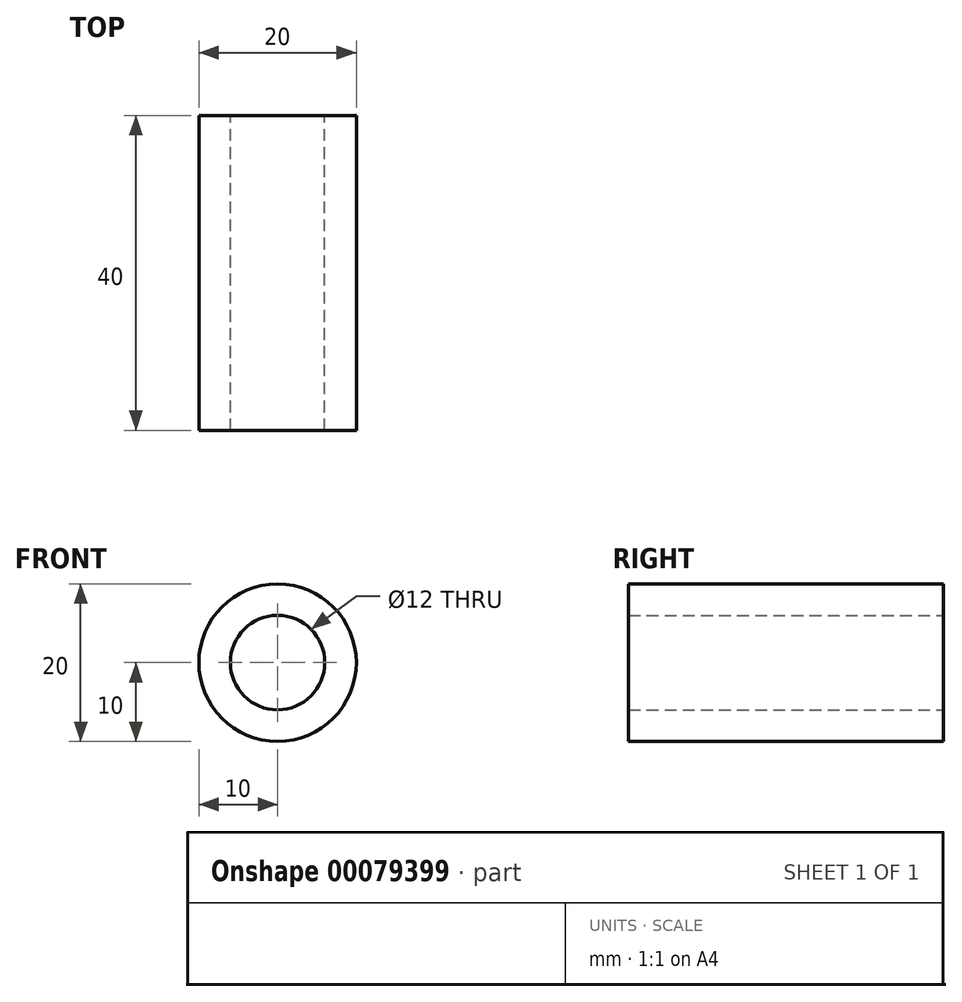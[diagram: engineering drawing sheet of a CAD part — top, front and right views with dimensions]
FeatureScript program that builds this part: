
annotation { "Feature Type Name" : "Feature", "Feature Type Description" : "" }
export const myFeature = defineFeature(function(context is Context, id is Id, definition is map)
    precondition{}
    {
        {
            var Q0;
            Q0=qCreatedBy(makeId("Front.planeOp"),FACE);
            var sketch = newSketch(context, id + "F0", { "sketchPlane" : qUnion([Q0])});
            skCircle(sketch, "E0", {"center": v(0, 0) * mm, "radius": 10 * mm});
            skCircle(sketch, "E1", {"center": v(0, 0) * mm, "radius": 6 * mm});
            skSolve(sketch);
        }
        {
            var Q0;
            Q0 = qSketchRegion(id + "F0", true);
            var Q1;
            Q1=makeQuery(id+"F0.imprint","IMPRINT",FACE,{"disambiguationData":[TD([[makeQuery(id+"F0.imprint","IMPRINT",EDGE,{"derivedFrom":sQuery(id+"F0.wireOp",EDGE,"E0")}),1.0]])]});
            extrude(context, id + "F1", {"entities" : qUnion([Q0, Q1]), "depth" : 40 * mm});
        }
    });
